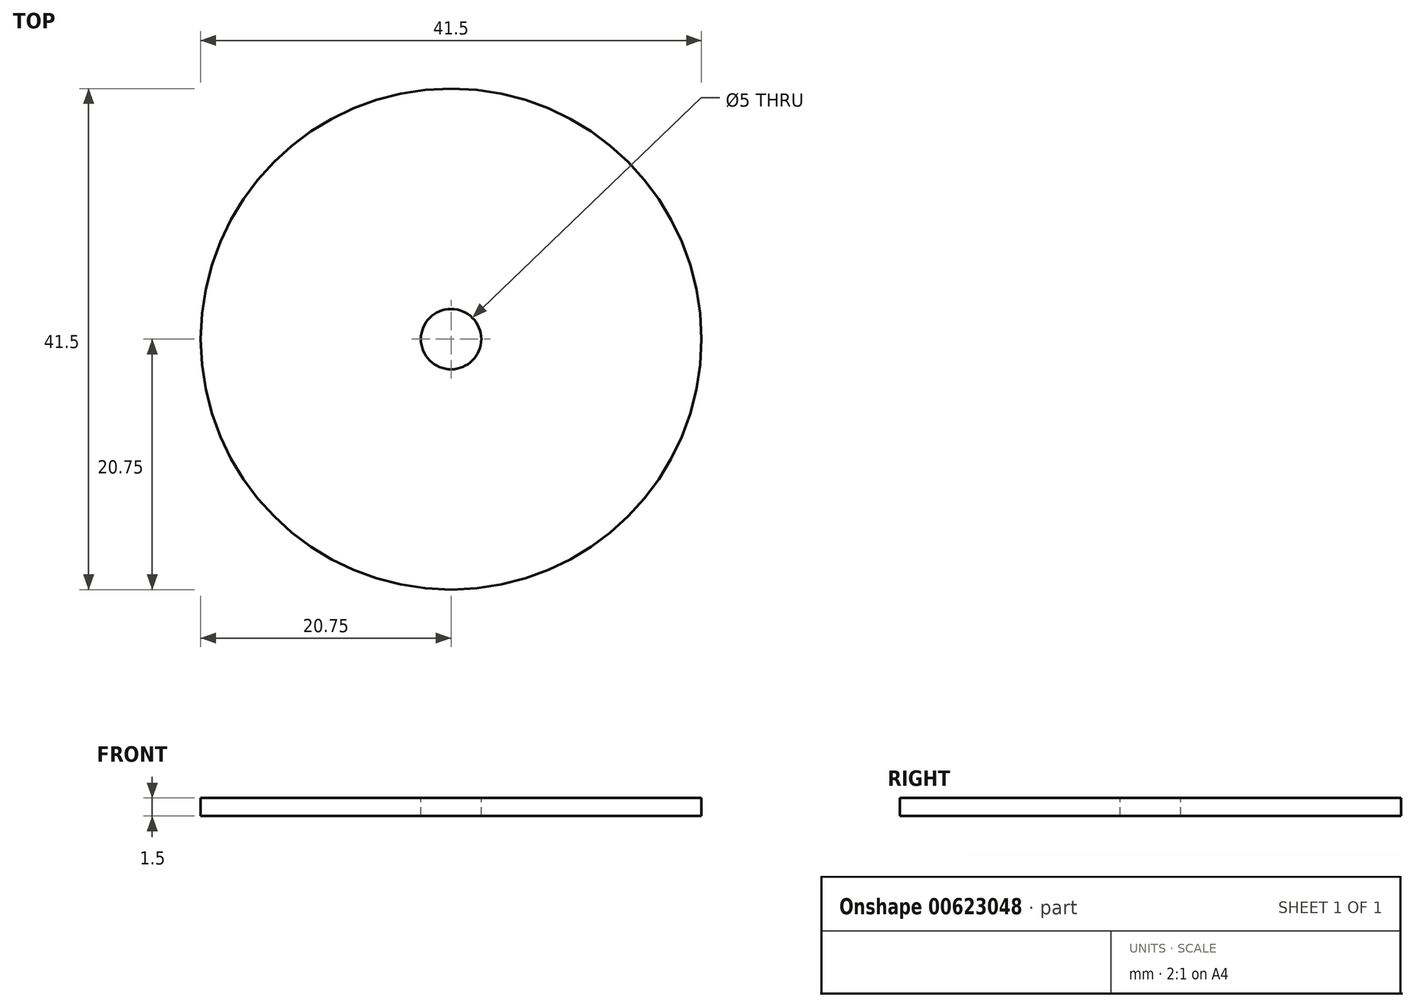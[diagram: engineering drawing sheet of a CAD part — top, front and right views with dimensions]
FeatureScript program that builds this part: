
annotation { "Feature Type Name" : "Feature", "Feature Type Description" : "" }
export const myFeature = defineFeature(function(context is Context, id is Id, definition is map)
    precondition{}
    {
        {
            var Q0;
            Q0=qCreatedBy(makeId("Top.planeOp"),FACE);
            var sketch = newSketch(context, id + "F0", { "sketchPlane" : qUnion([Q0])});
            skCircle(sketch, "E0", {"center": v(0, 0) * mm, "radius": 20.75 * mm});
            skSolve(sketch);
        }
        {
            var Q0;
            Q0=makeQuery(id+"F0.imprint","IMPRINT",FACE,{"disambiguationData":[TD([[makeQuery(id+"F0.imprint","IMPRINT",EDGE,{"derivedFrom":sQuery(id+"F0.wireOp",EDGE,"E0")}),1.0]])]});
            extrude(context, id + "F1", {"entities" : qUnion([Q0]), "depth" : 1.5 * mm, "offsetDistance" : 25 * mm});
        }
        {
            var Q0;
            Q0=makeQuery(id+"F1.opExtrude","CAP_FACE",FACE,{"disambiguationData":[OSD([sQuery(id+"F0.wireOp",EDGE,"E0")])],"isStart":false});
            var sketch = newSketch(context, id + "F2", { "sketchPlane" : qUnion([Q0])});
            skPoint(sketch, "E1", {"position": v(0, 0) * mm});
            skSolve(sketch);
        }
        {
            var Q0;
            Q0=sQuery(id+"F2.wireOp",VERTEX,"E1");
            var Q1;
            Q1=makeQuery(id+"F1.opExtrude","SWEPT_BODY",BODY,{"disambiguationData":[OSD([sQuery(id+"F0.wireOp",EDGE,"E0")])]});
            hole(context, id + "F3", {"style" : HoleStyle.SIMPLE, "endStyle" : HoleEndStyle.THROUGH, "holeDiameter" : 5 * mm, "majorDiameter" : 5 * mm, "isTappedThrough" : true, "tappedDepth" : 12 * mm, "tapClearance" : 3, "locations" : qUnion([Q0]), "scope" : qUnion([Q1])});
        }
    });
